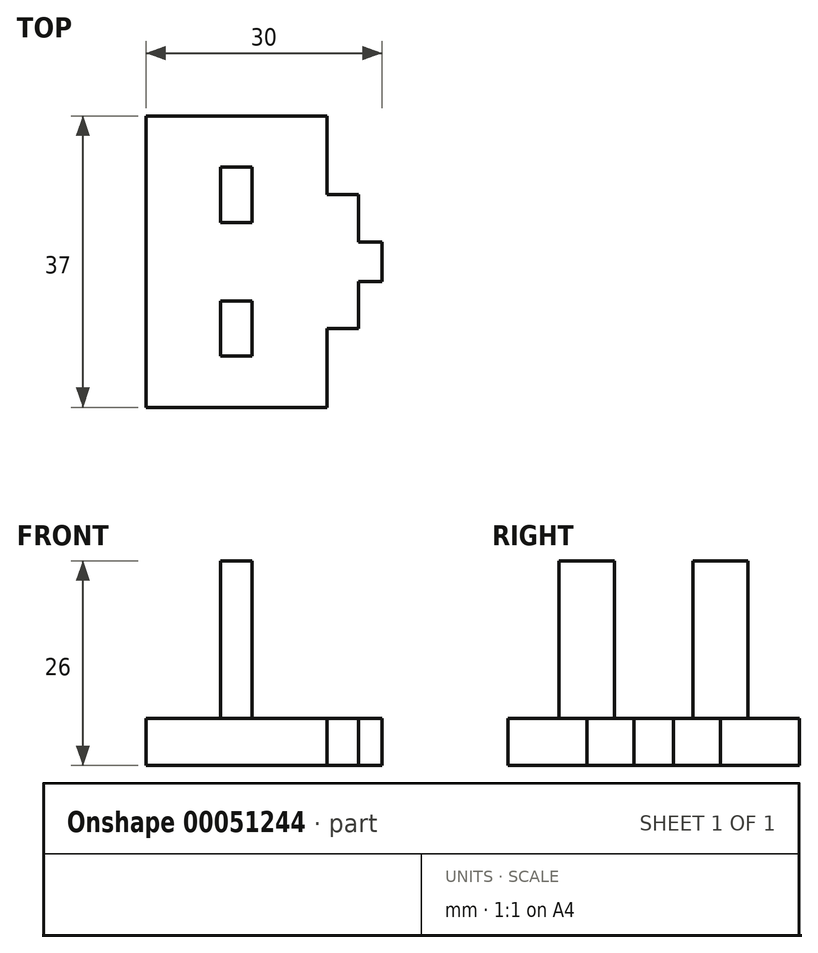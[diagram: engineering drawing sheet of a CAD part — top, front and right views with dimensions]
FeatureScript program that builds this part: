
annotation { "Feature Type Name" : "Feature", "Feature Type Description" : "" }
export const myFeature = defineFeature(function(context is Context, id is Id, definition is map)
    precondition{}
    {
        {
            var Q0;
            Q0=qCreatedBy(makeId("Top.planeOp"),FACE);
            var sketch = newSketch(context, id + "F0", { "sketchPlane" : qUnion([Q0])});
            skLineSegment(sketch, "E0.bottom", {"start": v(0, 0) * mm, "end": v(23, 0) * mm});
            skLineSegment(sketch, "E0.top", {"start": v(0, -37) * mm, "end": v(23, -37) * mm});
            skLineSegment(sketch, "E0.left", {"start": v(0, 0) * mm, "end": v(0, -37) * mm});
            skLineSegment(sketch, "E0.right", {"start": v(23, 0) * mm, "end": v(23, -37) * mm});
            skLineSegment(sketch, "E1.bottom", {"start": v(9.5, -6.5) * mm, "end": v(13.5, -6.5) * mm});
            skLineSegment(sketch, "E1.top", {"start": v(9.5, -13.5) * mm, "end": v(13.5, -13.5) * mm});
            skLineSegment(sketch, "E1.left", {"start": v(9.5, -6.5) * mm, "end": v(9.5, -13.5) * mm});
            skLineSegment(sketch, "E1.right", {"start": v(13.5, -6.5) * mm, "end": v(13.5, -13.5) * mm});
            skLineSegment(sketch, "E2.bottom", {"start": v(9.5, -23.5) * mm, "end": v(13.5, -23.5) * mm});
            skLineSegment(sketch, "E2.top", {"start": v(9.5, -30.5) * mm, "end": v(13.5, -30.5) * mm});
            skLineSegment(sketch, "E2.left", {"start": v(9.5, -23.5) * mm, "end": v(9.5, -30.5) * mm});
            skLineSegment(sketch, "E2.right", {"start": v(13.5, -23.5) * mm, "end": v(13.5, -30.5) * mm});
            skLineSegment(sketch, "E3.bottom", {"start": v(23, -10) * mm, "end": v(27, -10) * mm});
            skLineSegment(sketch, "E3.top", {"start": v(23, -27) * mm, "end": v(27, -27) * mm});
            skLineSegment(sketch, "E3.left", {"start": v(23, -10) * mm, "end": v(23, -27) * mm});
            skLineSegment(sketch, "E3.right", {"start": v(27, -10) * mm, "end": v(27, -27) * mm});
            skLineSegment(sketch, "E4.bottom", {"start": v(27, -16) * mm, "end": v(30, -16) * mm});
            skLineSegment(sketch, "E4.top", {"start": v(27, -21) * mm, "end": v(30, -21) * mm});
            skLineSegment(sketch, "E4.left", {"start": v(27, -16) * mm, "end": v(27, -21) * mm});
            skLineSegment(sketch, "E4.right", {"start": v(30, -16) * mm, "end": v(30, -21) * mm});
            skPoint(sketch, "E5", {"position": v(23, -18.5) * mm});
            skPoint(sketch, "E6", {"position": v(27, -18.5) * mm});
            skPoint(sketch, "E7", {"position": v(11.5, 0) * mm});
            skPoint(sketch, "E8", {"position": v(11.5, -6.5) * mm});
            skPoint(sketch, "E9", {"position": v(11.5, -23.5) * mm});
            skPoint(sketch, "E10", {"position": v(13.5, -10) * mm});
            skPoint(sketch, "E11", {"position": v(13.5, -27) * mm});
            skSolve(sketch);
        }
        {
            var Q0;
            {var subQ0=sQuery(id+"F0.wireOp",EDGE,"E0.bottom");Q0=makeQuery(id+"F0.imprint","IMPRINT",FACE,{"disambiguationData":[TD([[makeQuery(id+"F0.imprint","IMPRINT",EDGE,{"derivedFrom":subQ0}),-1.0]])]});}
            var Q1;
            {var subQ1=sQuery(id+"F0.wireOp",EDGE,"E3.bottom");Q1=makeQuery(id+"F0.imprint","IMPRINT",FACE,{"disambiguationData":[TD([[makeQuery(id+"F0.imprint","IMPRINT",EDGE,{"derivedFrom":subQ1}),-1.0]])]});}
            var Q2;
            Q2=makeQuery(id+"F0.imprint","IMPRINT",FACE,{"disambiguationData":[TD([[makeQuery(id+"F0.imprint","IMPRINT",EDGE,{"derivedFrom":sQuery(id+"F0.wireOp",EDGE,"E4.bottom")}),-1.0]])]});
            extrude(context, id + "F1", {"entities" : qUnion([Q0, Q1, Q2]), "depth" : 6 * mm});
        }
        {
            var Q0;
            Q0=makeQuery(id+"F0.imprint","IMPRINT",FACE,{"disambiguationData":[TD([[makeQuery(id+"F0.imprint","IMPRINT",EDGE,{"derivedFrom":sQuery(id+"F0.wireOp",EDGE,"E1.bottom")}),-1.0]])]});
            var Q1;
            Q1=makeQuery(id+"F0.imprint","IMPRINT",FACE,{"disambiguationData":[TD([[makeQuery(id+"F0.imprint","IMPRINT",EDGE,{"derivedFrom":sQuery(id+"F0.wireOp",EDGE,"E2.bottom")}),-1.0]])]});
            extrude(context, id + "F2", {"entities" : qUnion([Q0, Q1]), "operationType" : NewBodyOperationType.ADD, "depth" : 26 * mm});
        }
    });
